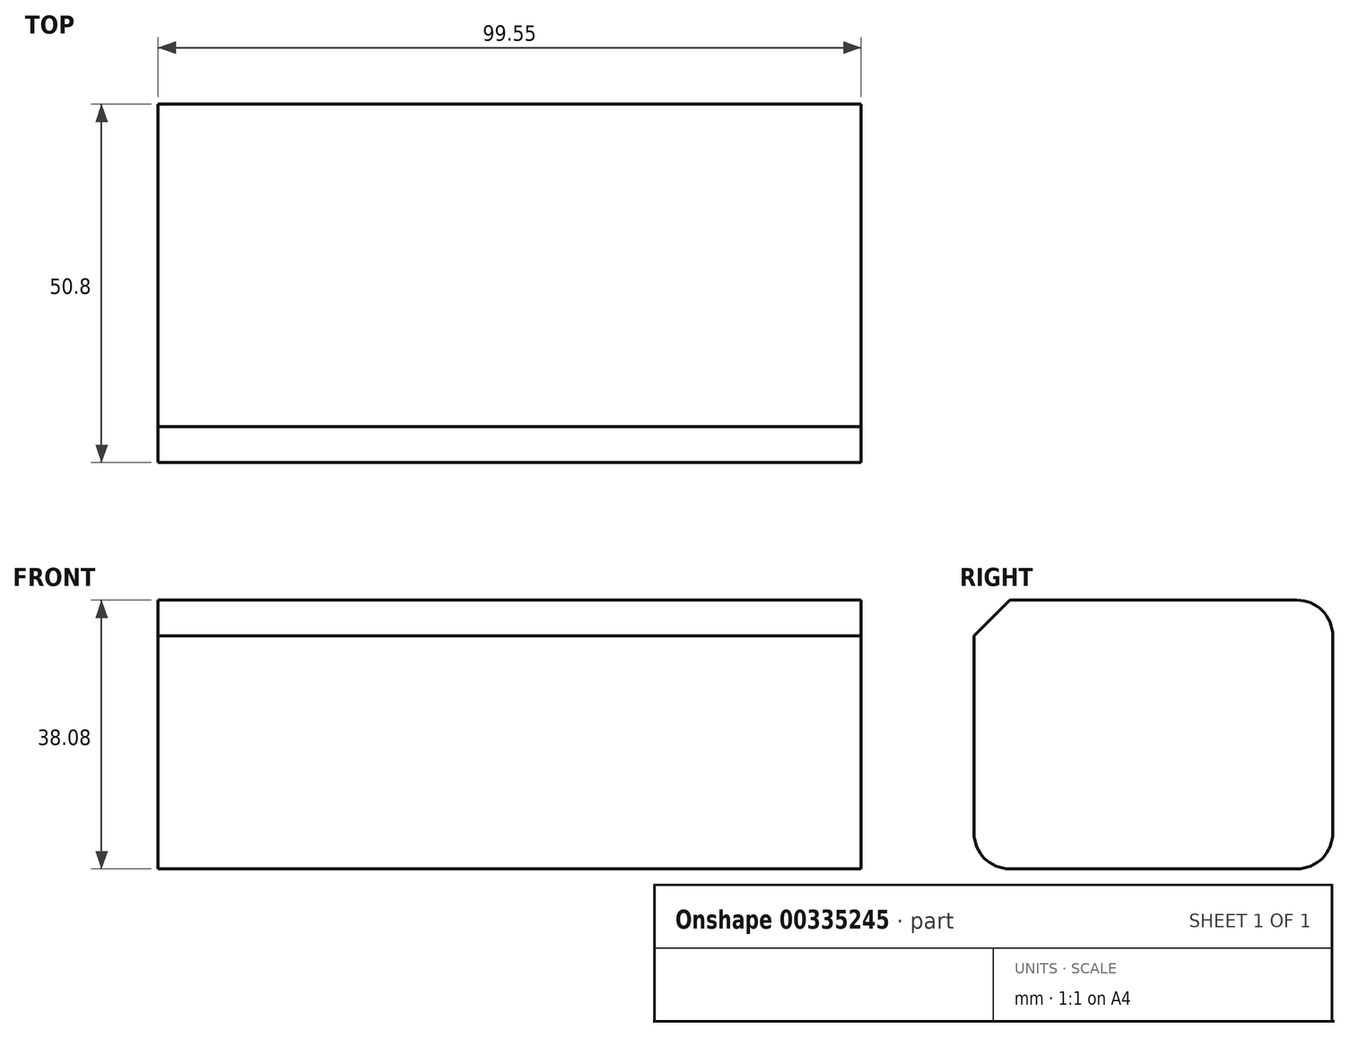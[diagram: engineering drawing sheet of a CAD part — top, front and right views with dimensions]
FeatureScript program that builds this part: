
annotation { "Feature Type Name" : "Feature", "Feature Type Description" : "" }
export const myFeature = defineFeature(function(context is Context, id is Id, definition is map)
    precondition{}
    {
        {
            var Q0;
            Q0=qCreatedBy(makeId("Front.planeOp"),FACE);
            var sketch = newSketch(context, id + "F0", { "sketchPlane" : qUnion([Q0])});
            skLineSegment(sketch, "E0.bottom", {"start": v(-45.1, 14.53) * mm, "end": v(54.45, 14.53) * mm});
            skLineSegment(sketch, "E0.top", {"start": v(-45.1, -23.55) * mm, "end": v(54.45, -23.55) * mm});
            skLineSegment(sketch, "E0.left", {"start": v(-45.1, 14.53) * mm, "end": v(-45.1, -23.55) * mm});
            skLineSegment(sketch, "E0.right", {"start": v(54.45, 14.53) * mm, "end": v(54.45, -23.55) * mm});
            skSolve(sketch);
        }
        {
            var Q0;
            Q0=makeQuery(id+"F0.imprint","IMPRINT",FACE,{"disambiguationData":[TD([[makeQuery(id+"F0.imprint","IMPRINT",EDGE,{"derivedFrom":sQuery(id+"F0.wireOp",EDGE,"E0.bottom")}),-1.0]])]});
            extrude(context, id + "F1", {"entities" : qUnion([Q0]), "depth" : 50.8 * mm});
        }
        {
            var Q0;
            Q0=makeQuery(id+"F1.opExtrude","CAP_EDGE",EDGE,{"disambiguationData":[OSD([sQuery(id+"F0.wireOp",EDGE,"E0.bottom")])],"isStart":false});
            chamfer(context, id + "F2", {"entities" : qUnion([Q0]), "width" : 5.08 * mm, "tangentPropagation" : true});
        }
        {
            var Q0;
            Q0=makeQuery(id+"F1.opExtrude","CAP_EDGE",EDGE,{"disambiguationData":[OSD([sQuery(id+"F0.wireOp",EDGE,"E0.bottom")])],"isStart":true});
            fillet(context, id + "F3", {"entities" : qUnion([Q0]), "radius" : 5.08 * mm, "tangentPropagation" : true, "allowEdgeOverflow" : false});
        }
        {
            var Q0;
            Q0=makeQuery(id+"F1.opExtrude","CAP_EDGE",EDGE,{"disambiguationData":[OSD([sQuery(id+"F0.wireOp",EDGE,"E0.top")])],"isStart":true});
            var Q1;
            Q1=makeQuery(id+"F1.opExtrude","CAP_EDGE",EDGE,{"disambiguationData":[OSD([sQuery(id+"F0.wireOp",EDGE,"E0.top")])],"isStart":false});
            fillet(context, id + "F4", {"entities" : qUnion([Q0, Q1]), "radius" : 5.08 * mm, "tangentPropagation" : true, "allowEdgeOverflow" : false});
        }
    });
